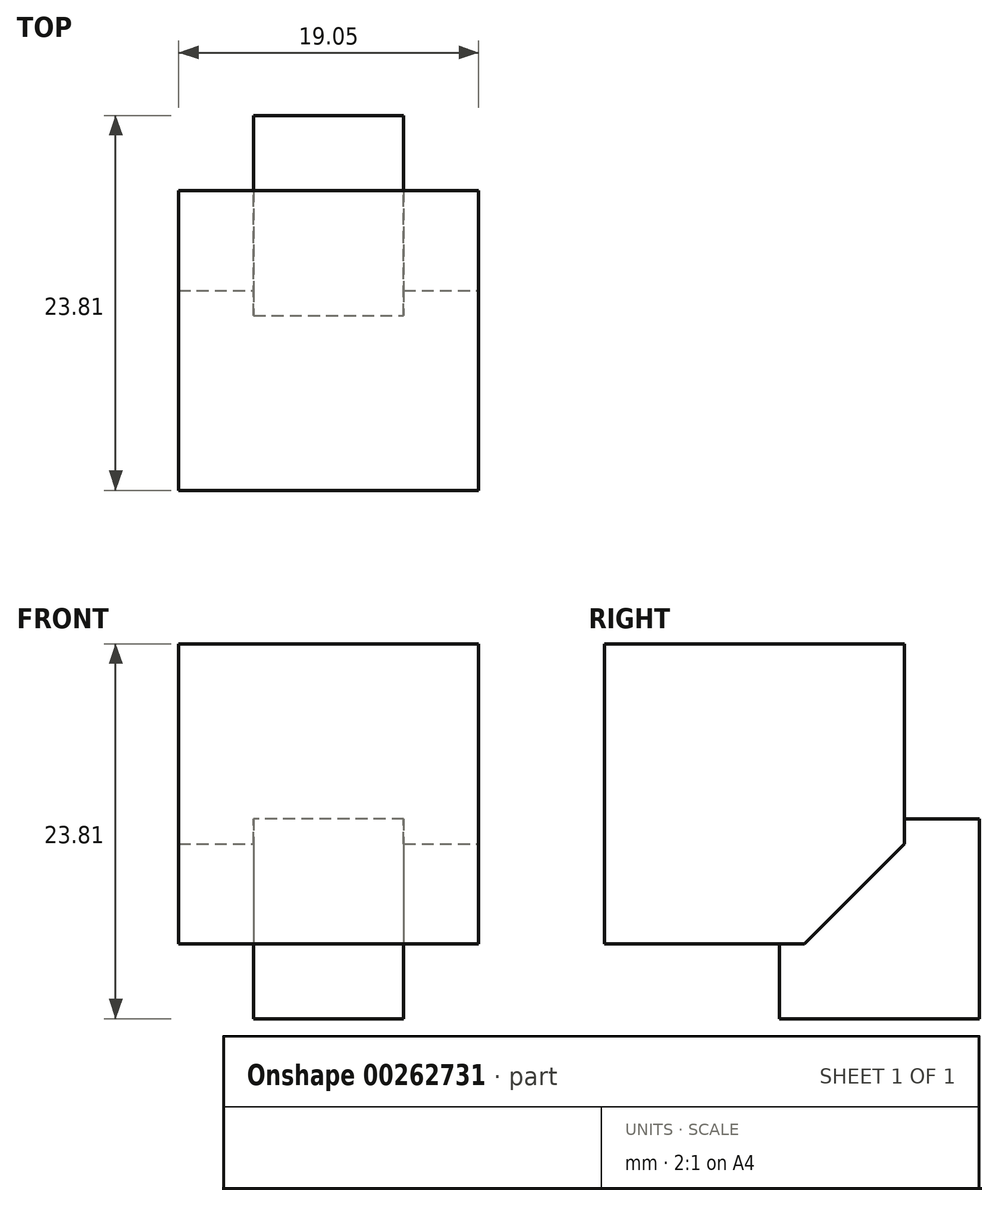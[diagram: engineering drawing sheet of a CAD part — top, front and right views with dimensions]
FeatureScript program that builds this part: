
annotation { "Feature Type Name" : "Feature", "Feature Type Description" : "" }
export const myFeature = defineFeature(function(context is Context, id is Id, definition is map)
    precondition{}
    {
        {
            var Q0;
            Q0=qCreatedBy(makeId("Front.planeOp"),FACE);
            var sketch = newSketch(context, id + "F0", { "sketchPlane" : qUnion([Q0])});
            skLineSegment(sketch, "E0.bottom", {"start": v(0, 0) * mm, "end": v(19.05, 0) * mm});
            skLineSegment(sketch, "E0.top", {"start": v(0, 19.05) * mm, "end": v(19.05, 19.05) * mm});
            skLineSegment(sketch, "E0.left", {"start": v(0, 0) * mm, "end": v(0, 19.05) * mm});
            skLineSegment(sketch, "E0.right", {"start": v(19.05, 0) * mm, "end": v(19.05, 19.05) * mm});
            skSolve(sketch);
        }
        {
            var Q0;
            Q0 = qSketchRegion(id + "F0", true);
            extrude(context, id + "F1", {"entities" : qUnion([Q0]), "oppositeDirection" : true, "depth" : 19.05 * mm});
        }
        {
            var Q0;
            Q0=makeQuery(id+"F1.opExtrude","SWEPT_FACE",FACE,{"disambiguationData":[OSD([sQuery(id+"F0.wireOp",EDGE,"E0.right")])]});
            cPlane(context, id + "F2", {"entities" : qUnion([Q0]), "cplaneType" : CPlaneType.OFFSET, "offset" : 9.52 * mm, "oppositeDirection" : true, "width" : 152.4 * mm, "height" : 152.4 * mm});
        }
        {
            var Q0;
            Q0=makeQuery(id+"F1.opExtrude","SWEPT_FACE",FACE,{"disambiguationData":[OSD([sQuery(id+"F0.wireOp",EDGE,"E0.right")])]});
            var sketch = newSketch(context, id + "F3", { "sketchPlane" : qUnion([Q0])});
            skLineSegment(sketch, "E1", {"start": v(12.7, 0) * mm, "end": v(19.05, 6.35) * mm});
            skLineSegment(sketch, "E2", {"start": v(19.05, 0) * mm, "end": v(12.7, 0) * mm});
            skSolve(sketch);
        }
        {
            var Q0;
            Q0 = qSketchRegion(id + "F3", true);
            var Q1;
            {var subQ0=sQuery(id+"F3.wireOp",EDGE,"E1");Q1=makeQuery(id+"F3.imprint","IMPRINT",FACE,{"disambiguationData":[TD([[makeQuery(id+"F3.imprint","IMPRINT",EDGE,{"derivedFrom":subQ0}),-1.0]])]});}
            extrude(context, id + "F4", {"entities" : qUnion([Q0, Q1]), "operationType" : NewBodyOperationType.REMOVE, "oppositeDirection" : true, "depth" : 19.05 * mm});
        }
        {
            var Q0;
            Q0=qCreatedBy(id+"F2.planeOp",FACE);
            var sketch = newSketch(context, id + "F5", { "sketchPlane" : qUnion([Q0])});
            skLineSegment(sketch, "E3.bottom", {"start": v(11.11, 7.94) * mm, "end": v(23.81, 7.94) * mm});
            skLineSegment(sketch, "E3.top", {"start": v(11.11, -4.76) * mm, "end": v(23.81, -4.76) * mm});
            skLineSegment(sketch, "E3.left", {"start": v(11.11, 7.94) * mm, "end": v(11.11, -4.76) * mm});
            skLineSegment(sketch, "E3.right", {"start": v(23.81, 7.94) * mm, "end": v(23.81, -4.76) * mm});
            skSolve(sketch);
        }
        {
            var Q0;
            Q0 = qSketchRegion(id + "F5", true);
            extrude(context, id + "F6", {"entities" : qUnion([Q0]), "operationType" : NewBodyOperationType.ADD, "endBound" : BoundingType.SYMMETRIC, "depth" : 9.52 * mm});
        }
    });
